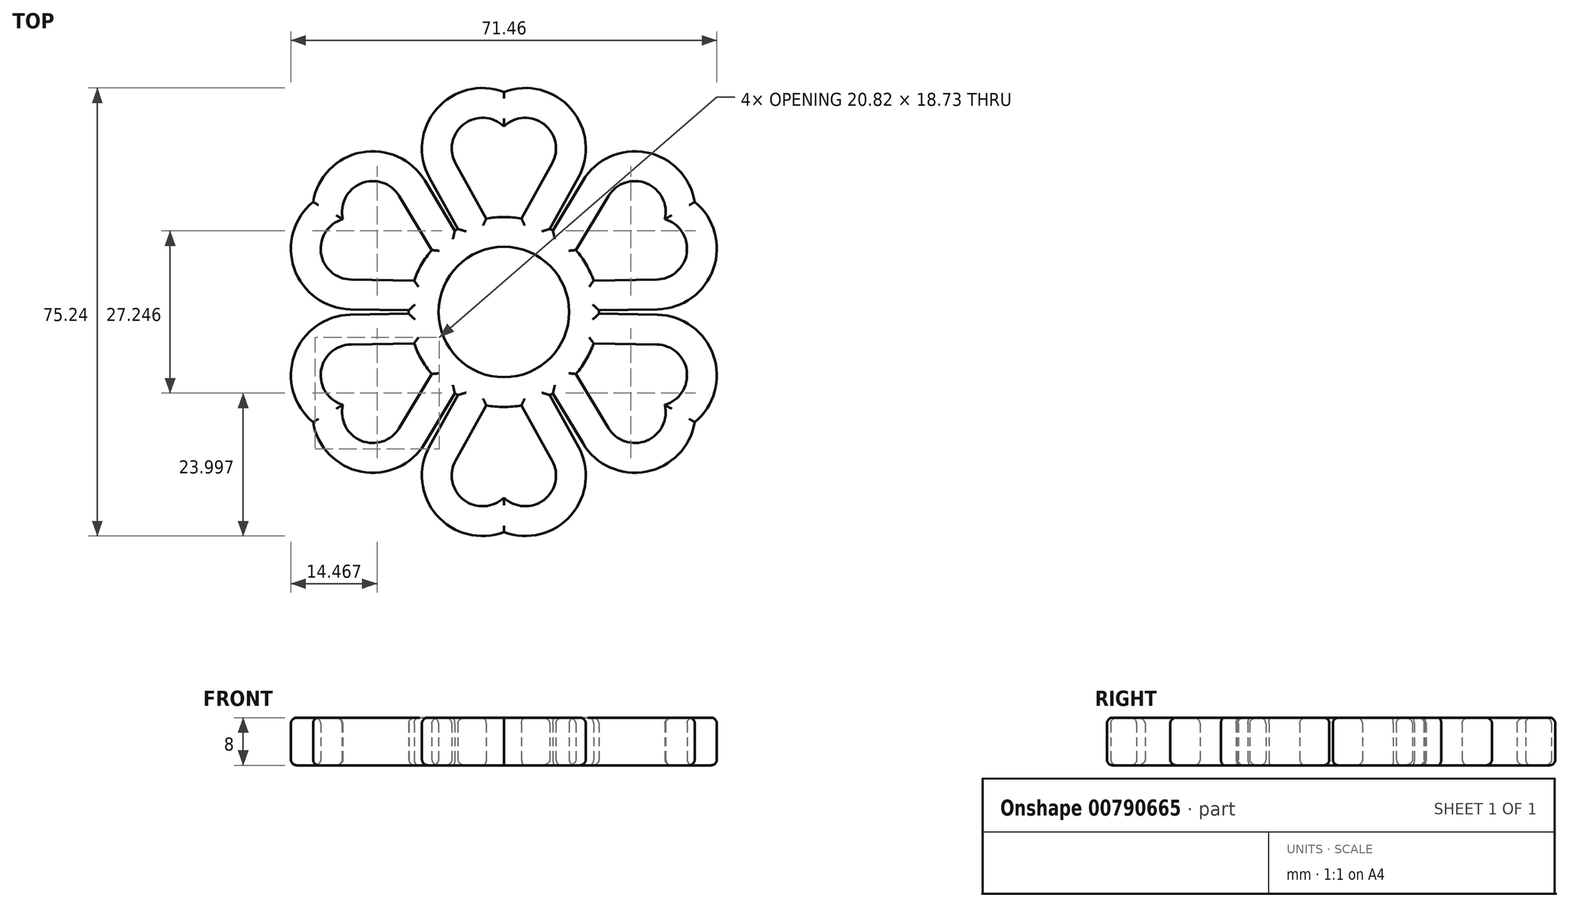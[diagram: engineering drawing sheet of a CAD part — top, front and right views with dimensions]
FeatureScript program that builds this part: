
annotation { "Feature Type Name" : "Feature", "Feature Type Description" : "" }
export const myFeature = defineFeature(function(context is Context, id is Id, definition is map)
    precondition{}
    {
        {
            var Q0;
            Q0=qCreatedBy(makeId("Top.planeOp"),FACE);
            var sketch = newSketch(context, id + "F0", { "sketchPlane" : qUnion([Q0]), "disableImprinting" : false});
            skCircle(sketch, "E0", {"center": v(0, 0) * mm, "radius": 10.95 * mm});
            skArc(sketch, "E1", {"start": v(0, 36.97) * mm, "mid": v(-11.27, 34.1) * mm, "end": v(-12.47, 22.52) * mm});
            skLineSegment(sketch, "E2", {"start": v(-12.47, 22.52) * mm, "end": v(-7.73, 13.95) * mm});
            skArc(sketch, "E3.MirrorC", {"start": v(0, 36.97) * mm, "mid": v(11.27, 34.1) * mm, "end": v(12.47, 22.52) * mm});
            skLineSegment(sketch, "E4.MirrorCS", {"start": v(12.47, 22.52) * mm, "end": v(7.73, 13.95) * mm});
            skCircle(sketch, "E5.0", {"center": v(0, 0) * mm, "radius": 15.95 * mm});
            skLineSegment(sketch, "E6.1.0", {"start": v(-25.74, 0.46) * mm, "end": v(-15.95, 0.28) * mm});
            skArc(sketch, "E6.1.1", {"start": v(-32.01, 18.48) * mm, "mid": v(-35.16, 7.28) * mm, "end": v(-25.74, 0.46) * mm});
            skArc(sketch, "E6.1.2", {"start": v(-32.01, 18.48) * mm, "mid": v(-23.89, 26.81) * mm, "end": v(-13.27, 22.06) * mm});
            skLineSegment(sketch, "E6.1.3", {"start": v(-13.27, 22.06) * mm, "end": v(-8.22, 13.67) * mm});
            skLineSegment(sketch, "E6.2.0", {"start": v(-13.27, -22.06) * mm, "end": v(-8.22, -13.67) * mm});
            skArc(sketch, "E6.2.1", {"start": v(-32.01, -18.48) * mm, "mid": v(-23.89, -26.81) * mm, "end": v(-13.27, -22.06) * mm});
            skArc(sketch, "E6.2.2", {"start": v(-32.01, -18.48) * mm, "mid": v(-35.16, -7.28) * mm, "end": v(-25.74, -0.46) * mm});
            skLineSegment(sketch, "E6.2.3", {"start": v(-25.74, -0.46) * mm, "end": v(-15.95, -0.28) * mm});
            skLineSegment(sketch, "E7.0", {"start": v(-8.1, 24.94) * mm, "end": v(-2.96, 15.67) * mm});
            skArc(sketch, "E7.1", {"start": v(0, 31.18) * mm, "mid": v(-6.73, 31.54) * mm, "end": v(-8.1, 24.94) * mm});
            skArc(sketch, "E7.2", {"start": v(0, 31.18) * mm, "mid": v(6.73, 31.54) * mm, "end": v(8.1, 24.94) * mm});
            skLineSegment(sketch, "E7.3", {"start": v(8.1, 24.94) * mm, "end": v(2.96, 15.67) * mm});
            skLineSegment(sketch, "E8.1.0", {"start": v(-25.65, 5.46) * mm, "end": v(-15.05, 5.27) * mm});
            skArc(sketch, "E8.1.1", {"start": v(-27, 15.59) * mm, "mid": v(-30.68, 9.94) * mm, "end": v(-25.65, 5.46) * mm});
            skArc(sketch, "E8.1.2", {"start": v(-27, 15.59) * mm, "mid": v(-23.95, 21.6) * mm, "end": v(-17.55, 19.49) * mm});
            skLineSegment(sketch, "E8.1.3", {"start": v(-17.55, 19.49) * mm, "end": v(-12.1, 10.4) * mm});
            skLineSegment(sketch, "E8.2.0", {"start": v(-17.55, -19.49) * mm, "end": v(-12.1, -10.4) * mm});
            skArc(sketch, "E8.2.1", {"start": v(-27, -15.59) * mm, "mid": v(-23.95, -21.6) * mm, "end": v(-17.55, -19.49) * mm});
            skArc(sketch, "E8.2.2", {"start": v(-27, -15.59) * mm, "mid": v(-30.68, -9.94) * mm, "end": v(-25.65, -5.46) * mm});
            skLineSegment(sketch, "E8.2.3", {"start": v(-25.65, -5.46) * mm, "end": v(-15.05, -5.27) * mm});
            skLineSegment(sketch, "E9.2.3.0", {"start": v(12.47, -22.52) * mm, "end": v(7.73, -13.95) * mm});
            skArc(sketch, "E9.3.3.0", {"start": v(0, -36.97) * mm, "mid": v(11.27, -34.1) * mm, "end": v(12.47, -22.52) * mm});
            skArc(sketch, "E9.7.3.0", {"start": v(0, -36.97) * mm, "mid": v(-11.27, -34.1) * mm, "end": v(-12.47, -22.52) * mm});
            skLineSegment(sketch, "E9.11.3.0", {"start": v(-12.47, -22.52) * mm, "end": v(-7.73, -13.95) * mm});
            skLineSegment(sketch, "E9.2.4.0", {"start": v(25.74, -0.46) * mm, "end": v(15.95, -0.28) * mm});
            skArc(sketch, "E9.3.4.0", {"start": v(32.01, -18.48) * mm, "mid": v(35.16, -7.28) * mm, "end": v(25.74, -0.46) * mm});
            skArc(sketch, "E9.7.4.0", {"start": v(32.01, -18.48) * mm, "mid": v(23.89, -26.81) * mm, "end": v(13.27, -22.06) * mm});
            skLineSegment(sketch, "E9.11.4.0", {"start": v(13.27, -22.06) * mm, "end": v(8.22, -13.67) * mm});
            skLineSegment(sketch, "E9.2.5.0", {"start": v(13.27, 22.06) * mm, "end": v(8.22, 13.67) * mm});
            skArc(sketch, "E9.3.5.0", {"start": v(32.01, 18.48) * mm, "mid": v(23.89, 26.81) * mm, "end": v(13.27, 22.06) * mm});
            skArc(sketch, "E9.7.5.0", {"start": v(32.01, 18.48) * mm, "mid": v(35.16, 7.28) * mm, "end": v(25.74, 0.46) * mm});
            skLineSegment(sketch, "E9.11.5.0", {"start": v(25.74, 0.46) * mm, "end": v(15.95, 0.28) * mm});
            skLineSegment(sketch, "E10.2.3.0", {"start": v(8.1, -24.94) * mm, "end": v(2.96, -15.67) * mm});
            skArc(sketch, "E10.3.3.0", {"start": v(0, -31.18) * mm, "mid": v(6.73, -31.54) * mm, "end": v(8.1, -24.94) * mm});
            skArc(sketch, "E10.7.3.0", {"start": v(0, -31.18) * mm, "mid": v(-6.73, -31.54) * mm, "end": v(-8.1, -24.94) * mm});
            skLineSegment(sketch, "E10.11.3.0", {"start": v(-8.1, -24.94) * mm, "end": v(-2.96, -15.67) * mm});
            skLineSegment(sketch, "E10.2.4.0", {"start": v(25.65, -5.46) * mm, "end": v(15.05, -5.27) * mm});
            skArc(sketch, "E10.3.4.0", {"start": v(27, -15.59) * mm, "mid": v(30.68, -9.94) * mm, "end": v(25.65, -5.46) * mm});
            skArc(sketch, "E10.7.4.0", {"start": v(27, -15.59) * mm, "mid": v(23.95, -21.6) * mm, "end": v(17.55, -19.49) * mm});
            skLineSegment(sketch, "E10.11.4.0", {"start": v(17.55, -19.49) * mm, "end": v(12.1, -10.4) * mm});
            skLineSegment(sketch, "E10.2.5.0", {"start": v(17.55, 19.49) * mm, "end": v(12.1, 10.4) * mm});
            skArc(sketch, "E10.3.5.0", {"start": v(27, 15.59) * mm, "mid": v(23.95, 21.6) * mm, "end": v(17.55, 19.49) * mm});
            skArc(sketch, "E10.7.5.0", {"start": v(27, 15.59) * mm, "mid": v(30.68, 9.94) * mm, "end": v(25.65, 5.46) * mm});
            skLineSegment(sketch, "E10.11.5.0", {"start": v(25.65, 5.46) * mm, "end": v(15.05, 5.27) * mm});
            skSolve(sketch);
        }
        {
            var Q0;
            Q0 = qSketchRegion(id + "F0", true);
            extrude(context, id + "F1", {"entities" : qUnion([Q0]), "depth" : 8 * mm, "offsetDistance" : 25 * mm});
        }
        {
            var Q0;
            {var subQ0=sQuery(id+"F0.wireOp",EDGE,"E5.0");Q0=makeQuery(id+"F1.opExtrude","CAP_EDGE",EDGE,{"disambiguationData":[OSD([subQ0]),TDD([makeQuery(id+"F0.imprint","IMPRINT",EDGE,{"disambiguationData":[TD([[makeQuery(id+"F0.imprint","INTERSECT",VERTEX,{"derivedFrom":[sQuery(id+"F0.wireOp",EDGE,"E4.MirrorCS"),subQ0]}),1.0]])],"derivedFrom":subQ0})])],"isStart":false});}
            var Q1;
            {var subQ0=sQuery(id+"F0.wireOp",EDGE,"E5.0");Q1=makeQuery(id+"F1.opExtrude","CAP_EDGE",EDGE,{"disambiguationData":[OSD([subQ0]),TDD([makeQuery(id+"F0.imprint","IMPRINT",EDGE,{"disambiguationData":[TD([[makeQuery(id+"F0.imprint","INTERSECT",VERTEX,{"derivedFrom":[sQuery(id+"F0.wireOp",EDGE,"E2"),subQ0]}),-1.0]])],"derivedFrom":subQ0})])],"isStart":true});}
            var Q2;
            {var subQ0=sQuery(id+"F0.wireOp",EDGE,"E5.0");Q2=makeQuery(id+"F1.opExtrude","CAP_EDGE",EDGE,{"disambiguationData":[OSD([subQ0]),TDD([makeQuery(id+"F0.imprint","IMPRINT",EDGE,{"disambiguationData":[TD([[makeQuery(id+"F0.imprint","INTERSECT",VERTEX,{"derivedFrom":[sQuery(id+"F0.wireOp",EDGE,"E4.MirrorCS"),subQ0]}),1.0]])],"derivedFrom":subQ0})])],"isStart":true});}
            var Q3;
            Q3=makeQuery(id+"F1.opExtrude","CAP_EDGE",EDGE,{"disambiguationData":[OSD([sQuery(id+"F0.wireOp",EDGE,"E8.2.3")])],"isStart":false});
            var Q4;
            Q4=makeQuery(id+"F1.opExtrude","SWEPT_EDGE",EDGE,{"disambiguationData":[OSD([sQuery(id+"F0.wireOp",EDGE,"E6.1.0"),sQuery(id+"F0.wireOp",EDGE,"E6.1.1")])]});
            var Q5;
            Q5=makeQuery(id+"F1.opExtrude","CAP_EDGE",EDGE,{"disambiguationData":[OSD([sQuery(id+"F0.wireOp",EDGE,"E8.1.1")])],"isStart":true});
            var Q6;
            Q6=makeQuery(id+"F1.opExtrude","SWEPT_EDGE",EDGE,{"disambiguationData":[OSD([sQuery(id+"F0.wireOp",EDGE,"E8.1.0"),sQuery(id+"F0.wireOp",EDGE,"E8.1.1")])]});
            var Q7;
            Q7=makeQuery(id+"F1.opExtrude","CAP_EDGE",EDGE,{"disambiguationData":[OSD([sQuery(id+"F0.wireOp",EDGE,"E8.2.1")])],"isStart":false});
            var Q8;
            Q8=makeQuery(id+"F1.opExtrude","CAP_FACE",FACE,{"disambiguationData":[OSD([sQuery(id+"F0.wireOp",EDGE,"E0"),sQuery(id+"F0.wireOp",EDGE,"E1"),sQuery(id+"F0.wireOp",EDGE,"E2"),sQuery(id+"F0.wireOp",EDGE,"E3.MirrorC"),sQuery(id+"F0.wireOp",EDGE,"E4.MirrorCS"),sQuery(id+"F0.wireOp",EDGE,"E5.0"),sQuery(id+"F0.wireOp",EDGE,"E6.1.0"),sQuery(id+"F0.wireOp",EDGE,"E6.1.1"),sQuery(id+"F0.wireOp",EDGE,"E6.1.2"),sQuery(id+"F0.wireOp",EDGE,"E6.1.3"),sQuery(id+"F0.wireOp",EDGE,"E6.2.0"),sQuery(id+"F0.wireOp",EDGE,"E6.2.1"),sQuery(id+"F0.wireOp",EDGE,"E6.2.2"),sQuery(id+"F0.wireOp",EDGE,"E6.2.3"),sQuery(id+"F0.wireOp",EDGE,"E7.0"),sQuery(id+"F0.wireOp",EDGE,"E7.1"),sQuery(id+"F0.wireOp",EDGE,"E7.2"),sQuery(id+"F0.wireOp",EDGE,"E7.3"),sQuery(id+"F0.wireOp",EDGE,"E8.1.0"),sQuery(id+"F0.wireOp",EDGE,"E8.1.1"),sQuery(id+"F0.wireOp",EDGE,"E8.1.2"),sQuery(id+"F0.wireOp",EDGE,"E8.1.3"),sQuery(id+"F0.wireOp",EDGE,"E8.2.0"),sQuery(id+"F0.wireOp",EDGE,"E8.2.1"),sQuery(id+"F0.wireOp",EDGE,"E8.2.2"),sQuery(id+"F0.wireOp",EDGE,"E8.2.3"),sQuery(id+"F0.wireOp",EDGE,"E9.2.3.0"),sQuery(id+"F0.wireOp",EDGE,"E9.3.3.0"),sQuery(id+"F0.wireOp",EDGE,"E9.7.3.0"),sQuery(id+"F0.wireOp",EDGE,"E9.11.3.0"),sQuery(id+"F0.wireOp",EDGE,"E9.2.4.0"),sQuery(id+"F0.wireOp",EDGE,"E9.3.4.0"),sQuery(id+"F0.wireOp",EDGE,"E9.7.4.0"),sQuery(id+"F0.wireOp",EDGE,"E9.11.4.0"),sQuery(id+"F0.wireOp",EDGE,"E9.2.5.0"),sQuery(id+"F0.wireOp",EDGE,"E9.3.5.0"),sQuery(id+"F0.wireOp",EDGE,"E9.7.5.0"),sQuery(id+"F0.wireOp",EDGE,"E9.11.5.0"),sQuery(id+"F0.wireOp",EDGE,"E10.2.3.0"),sQuery(id+"F0.wireOp",EDGE,"E10.3.3.0"),sQuery(id+"F0.wireOp",EDGE,"E10.7.3.0"),sQuery(id+"F0.wireOp",EDGE,"E10.11.3.0"),sQuery(id+"F0.wireOp",EDGE,"E10.2.4.0"),sQuery(id+"F0.wireOp",EDGE,"E10.3.4.0"),sQuery(id+"F0.wireOp",EDGE,"E10.7.4.0"),sQuery(id+"F0.wireOp",EDGE,"E10.11.4.0"),sQuery(id+"F0.wireOp",EDGE,"E10.2.5.0"),sQuery(id+"F0.wireOp",EDGE,"E10.3.5.0"),sQuery(id+"F0.wireOp",EDGE,"E10.7.5.0"),sQuery(id+"F0.wireOp",EDGE,"E10.11.5.0")])],"isStart":false});
            var Q9;
            {var subQ0=sQuery(id+"F0.wireOp",EDGE,"E5.0");Q9=makeQuery(id+"F1.opExtrude","CAP_EDGE",EDGE,{"disambiguationData":[OSD([subQ0]),TDD([makeQuery(id+"F0.imprint","IMPRINT",EDGE,{"disambiguationData":[TD([[makeQuery(id+"F0.imprint","INTERSECT",VERTEX,{"derivedFrom":[subQ0,sQuery(id+"F0.wireOp",EDGE,"E8.2.0")]}),1.0]])],"derivedFrom":subQ0})])],"isStart":false});}
            var Q10;
            Q10=makeQuery(id+"F1.opExtrude","CAP_FACE",FACE,{"disambiguationData":[OSD([sQuery(id+"F0.wireOp",EDGE,"E0"),sQuery(id+"F0.wireOp",EDGE,"E1"),sQuery(id+"F0.wireOp",EDGE,"E2"),sQuery(id+"F0.wireOp",EDGE,"E3.MirrorC"),sQuery(id+"F0.wireOp",EDGE,"E4.MirrorCS"),sQuery(id+"F0.wireOp",EDGE,"E5.0"),sQuery(id+"F0.wireOp",EDGE,"E6.1.0"),sQuery(id+"F0.wireOp",EDGE,"E6.1.1"),sQuery(id+"F0.wireOp",EDGE,"E6.1.2"),sQuery(id+"F0.wireOp",EDGE,"E6.1.3"),sQuery(id+"F0.wireOp",EDGE,"E6.2.0"),sQuery(id+"F0.wireOp",EDGE,"E6.2.1"),sQuery(id+"F0.wireOp",EDGE,"E6.2.2"),sQuery(id+"F0.wireOp",EDGE,"E6.2.3"),sQuery(id+"F0.wireOp",EDGE,"E7.0"),sQuery(id+"F0.wireOp",EDGE,"E7.1"),sQuery(id+"F0.wireOp",EDGE,"E7.2"),sQuery(id+"F0.wireOp",EDGE,"E7.3"),sQuery(id+"F0.wireOp",EDGE,"E8.1.0"),sQuery(id+"F0.wireOp",EDGE,"E8.1.1"),sQuery(id+"F0.wireOp",EDGE,"E8.1.2"),sQuery(id+"F0.wireOp",EDGE,"E8.1.3"),sQuery(id+"F0.wireOp",EDGE,"E8.2.0"),sQuery(id+"F0.wireOp",EDGE,"E8.2.1"),sQuery(id+"F0.wireOp",EDGE,"E8.2.2"),sQuery(id+"F0.wireOp",EDGE,"E8.2.3"),sQuery(id+"F0.wireOp",EDGE,"E9.2.3.0"),sQuery(id+"F0.wireOp",EDGE,"E9.3.3.0"),sQuery(id+"F0.wireOp",EDGE,"E9.7.3.0"),sQuery(id+"F0.wireOp",EDGE,"E9.11.3.0"),sQuery(id+"F0.wireOp",EDGE,"E9.2.4.0"),sQuery(id+"F0.wireOp",EDGE,"E9.3.4.0"),sQuery(id+"F0.wireOp",EDGE,"E9.7.4.0"),sQuery(id+"F0.wireOp",EDGE,"E9.11.4.0"),sQuery(id+"F0.wireOp",EDGE,"E9.2.5.0"),sQuery(id+"F0.wireOp",EDGE,"E9.3.5.0"),sQuery(id+"F0.wireOp",EDGE,"E9.7.5.0"),sQuery(id+"F0.wireOp",EDGE,"E9.11.5.0"),sQuery(id+"F0.wireOp",EDGE,"E10.2.3.0"),sQuery(id+"F0.wireOp",EDGE,"E10.3.3.0"),sQuery(id+"F0.wireOp",EDGE,"E10.7.3.0"),sQuery(id+"F0.wireOp",EDGE,"E10.11.3.0"),sQuery(id+"F0.wireOp",EDGE,"E10.2.4.0"),sQuery(id+"F0.wireOp",EDGE,"E10.3.4.0"),sQuery(id+"F0.wireOp",EDGE,"E10.7.4.0"),sQuery(id+"F0.wireOp",EDGE,"E10.11.4.0"),sQuery(id+"F0.wireOp",EDGE,"E10.2.5.0"),sQuery(id+"F0.wireOp",EDGE,"E10.3.5.0"),sQuery(id+"F0.wireOp",EDGE,"E10.7.5.0"),sQuery(id+"F0.wireOp",EDGE,"E10.11.5.0")])],"isStart":true});
            fillet(context, id + "F2", {"entities" : qUnion([Q0, Q1, Q2, Q3, Q4, Q5, Q6, Q7, Q8, Q9, Q10]), "radius" : 1 * mm, "tangentPropagation" : true, "allowEdgeOverflow" : false});
        }
    });
